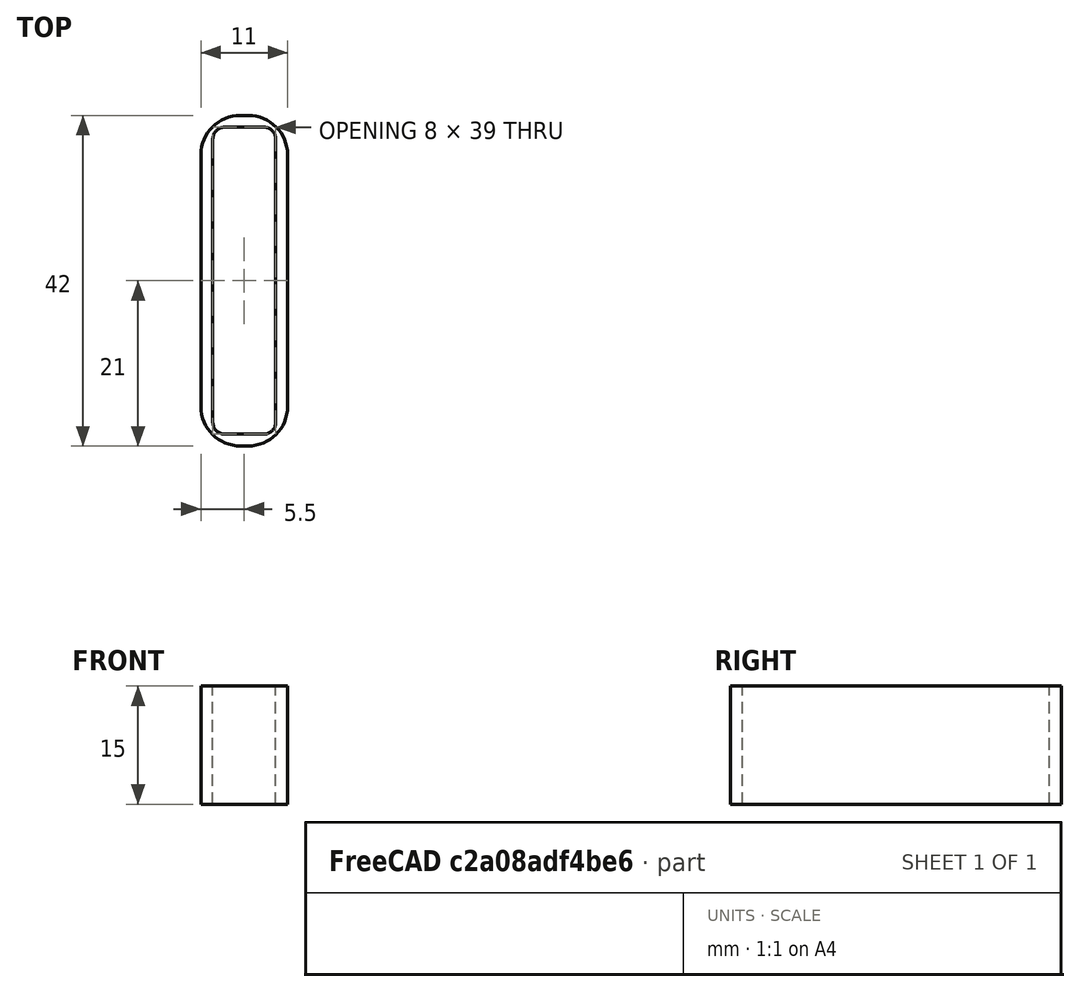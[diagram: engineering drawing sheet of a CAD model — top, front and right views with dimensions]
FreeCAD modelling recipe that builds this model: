
FCSTD DOCUMENT  (FreeCAD 1.0RUnknown)
Label: Belt-holder-v2
License: All rights reserved
LicenseURL: https://en.wikipedia.org/wiki/All_rights_reserved
objects: Sketcher::SketchObject×1, PartDesign::Pad×1, PartDesign::Body×1
note: 6 computed .brp shape members not serialized (recipe doc carries the construction recipe); baked Part::Feature solids carry a one-line shape summary decoded from their .brp

FEATURE [Sketcher::SketchObject] Sketch
  ArcFitTolerance = 1e-06
  AttachmentSupport = -> [XY_Plane]
  FullyConstrained = true
  MakeInternals = false
  MapMode = 5
  sketch-geometry (24):
    g0: LineSegment StartX=5 StartY=7.02e-14 StartZ=0 EndX=6 EndY=7.02e-14 EndZ=0
    g1: LineSegment StartX=11 StartY=5 StartZ=0 EndX=11 EndY=37 EndZ=0
    g2: LineSegment StartX=6 StartY=42 StartZ=0 EndX=5 EndY=42 EndZ=0
    g3: LineSegment StartX=7.11e-14 StartY=37 StartZ=0 EndX=7.11e-14 EndY=5 EndZ=0
    g4: LineSegment StartX=3 StartY=1.5 StartZ=0 EndX=8 EndY=1.5 EndZ=0
    g5: LineSegment StartX=9.5 StartY=3 StartZ=0 EndX=9.5 EndY=39 EndZ=0
    g6: LineSegment StartX=8 StartY=40.5 StartZ=0 EndX=3 EndY=40.5 EndZ=0
    g7: LineSegment StartX=1.5 StartY=39 StartZ=0 EndX=1.5 EndY=3 EndZ=0
    g8: ArcOfCircle CenterX=5 CenterY=37 CenterZ=0 NormalX=0 NormalY=0 NormalZ=1 AngleXU=0 Radius=5 StartAngle=1.5708 EndAngle=3.14159
    g9: GeomPoint [constr] X=0 Y=42 Z=0
    g10: ArcOfCircle CenterX=6 CenterY=37 CenterZ=0 NormalX=0 NormalY=0 NormalZ=1 AngleXU=0 Radius=5 StartAngle=1.132e-13 EndAngle=1.5708
    g11: GeomPoint [constr] X=11 Y=42 Z=0
    g12: ArcOfCircle CenterX=8 CenterY=39 CenterZ=0 NormalX=0 NormalY=0 NormalZ=1 AngleXU=0 Radius=1.5 StartAngle=0 EndAngle=1.5708
    g13: GeomPoint [constr] X=9.5 Y=40.5 Z=0
    g14: ArcOfCircle CenterX=3 CenterY=39 CenterZ=0 NormalX=0 NormalY=0 NormalZ=1 AngleXU=0 Radius=1.5 StartAngle=1.5708 EndAngle=3.14159
    g15: GeomPoint [constr] X=1.5 Y=40.5 Z=0
    g16: ArcOfCircle CenterX=3 CenterY=3 CenterZ=0 NormalX=0 NormalY=0 NormalZ=1 AngleXU=0 Radius=1.5 StartAngle=3.14159 EndAngle=4.71239
    g17: GeomPoint [constr] X=1.5 Y=1.5 Z=0
    g18: ArcOfCircle CenterX=8 CenterY=3 CenterZ=0 NormalX=0 NormalY=0 NormalZ=1 AngleXU=0 Radius=1.5 StartAngle=4.71239 EndAngle=6.28319
    g19: GeomPoint [constr] X=9.5 Y=1.5 Z=0
    g20: ArcOfCircle CenterX=5 CenterY=5 CenterZ=0 NormalX=0 NormalY=0 NormalZ=1 AngleXU=0 Radius=5 StartAngle=3.14159 EndAngle=4.71239
    g21: GeomPoint [constr] X=0 Y=0 Z=0
    g22: ArcOfCircle CenterX=6 CenterY=5 CenterZ=0 NormalX=0 NormalY=0 NormalZ=1 AngleXU=0 Radius=5 StartAngle=4.71239 EndAngle=6.28319
    g23: GeomPoint [constr] X=11 Y=0 Z=0
  constraints (55):
    c: Horizontal(g0)
    c: Horizontal(g2)
    c: Vertical(g1)
    c: Vertical(g3)
    c: Coincident(g21,g-1)
    c: Horizontal(g4)
    c: Horizontal(g6)
    c: Vertical(g5)
    c: Vertical(g7)
    c: DistanceX(g17,g19) = 8
    c: DistanceY(g17,g15) = 39
    c: Distance(g9,g7) = 1.5
    c: Distance(g19,g1) = 1.5
    c: Distance(g21,g4) = 1.5
    c: Distance(g13,g2) = 1.5
    c: PointOnObject(g9,g3)
    c: PointOnObject(g9,g2)
    c: Tangent(g3,g8) = -1.5708
    c: Tangent(g2,g8) = -1.5708
    c: PointOnObject(g11,g2)
    c: PointOnObject(g11,g1)
    c: Tangent(g2,g10) = -1.5708
    c: Tangent(g1,g10) = -1.5708
    c: PointOnObject(g13,g6)
    c: PointOnObject(g13,g5)
    c: Tangent(g6,g12) = -1.5708
    c: Tangent(g5,g12) = -1.5708
    c: PointOnObject(g15,g7)
    c: PointOnObject(g15,g6)
    c: Tangent(g7,g14) = -1.5708
    c: Tangent(g6,g14) = -1.5708
    c: PointOnObject(g17,g7)
    c: PointOnObject(g17,g4)
    c: Tangent(g7,g16) = -1.5708
    c: Tangent(g4,g16) = -1.5708
    c: PointOnObject(g19,g5)
    c: PointOnObject(g19,g4)
    c: Tangent(g5,g18) = -1.5708
    c: Tangent(g4,g18) = -1.5708
    c: PointOnObject(g21,g3)
    c: PointOnObject(g21,g0)
    c: Tangent(g3,g20) = -1.5708
    c: Tangent(g0,g20) = -1.5708
    c: Equal(g14,g12)
    c: Equal(g12,g18)
    c: Equal(g18,g16)
    c: Radius(g18) = 1.5
    c: PointOnObject(g23,g1)
    c: PointOnObject(g23,g0)
    c: Tangent(g1,g22) = -1.5708
    c: Tangent(g0,g22) = -1.5708
    c: Equal(g8,g10)
    c: Equal(g10,g22)
    c: Equal(g22,g20)
    c: Radius(g10) = 5
FEATURE [PartDesign::Pad] Pad
  Direction = (0,0,1)
  Length = 15
  Length2 = 10
  Profile = -> Sketch
  ReferenceAxis = -> Sketch [N_Axis]
  Refine = true
  Suppressed = false
  Type = 0
FEATURE [PartDesign::Body] Body
  AllowCompound = false
  Group = -> [Sketch,Pad]
  Origin = -> Origin
  Tip = -> Pad
